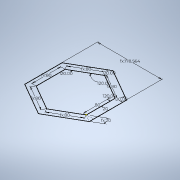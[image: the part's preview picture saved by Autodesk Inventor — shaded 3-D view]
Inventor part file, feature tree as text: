
AUTODESK INVENTOR PART (.ipt)
format: ipt  version: 2020 (Build 240168000, 168)  size: 102,400 bytes
history: native  units: mm
features: sketch x1
ambient origin geometry x8: Origin, YZ Plane, XZ Plane, XY Plane, X Axis, Y Axis, Z Axis, Center Point
feature tree (1):
  sketch  "Sketch1"  dims[d0=80.0mm d1=80.0mm d2=80.0mm d3=80.0mm d4=80.0mm d5=80.0mm d6=120.0deg d7=120.0deg d8=120.0deg d9=120.0deg d10=120.0deg d11=20.0mm d12=20.0mm d13=178.564065mm]
